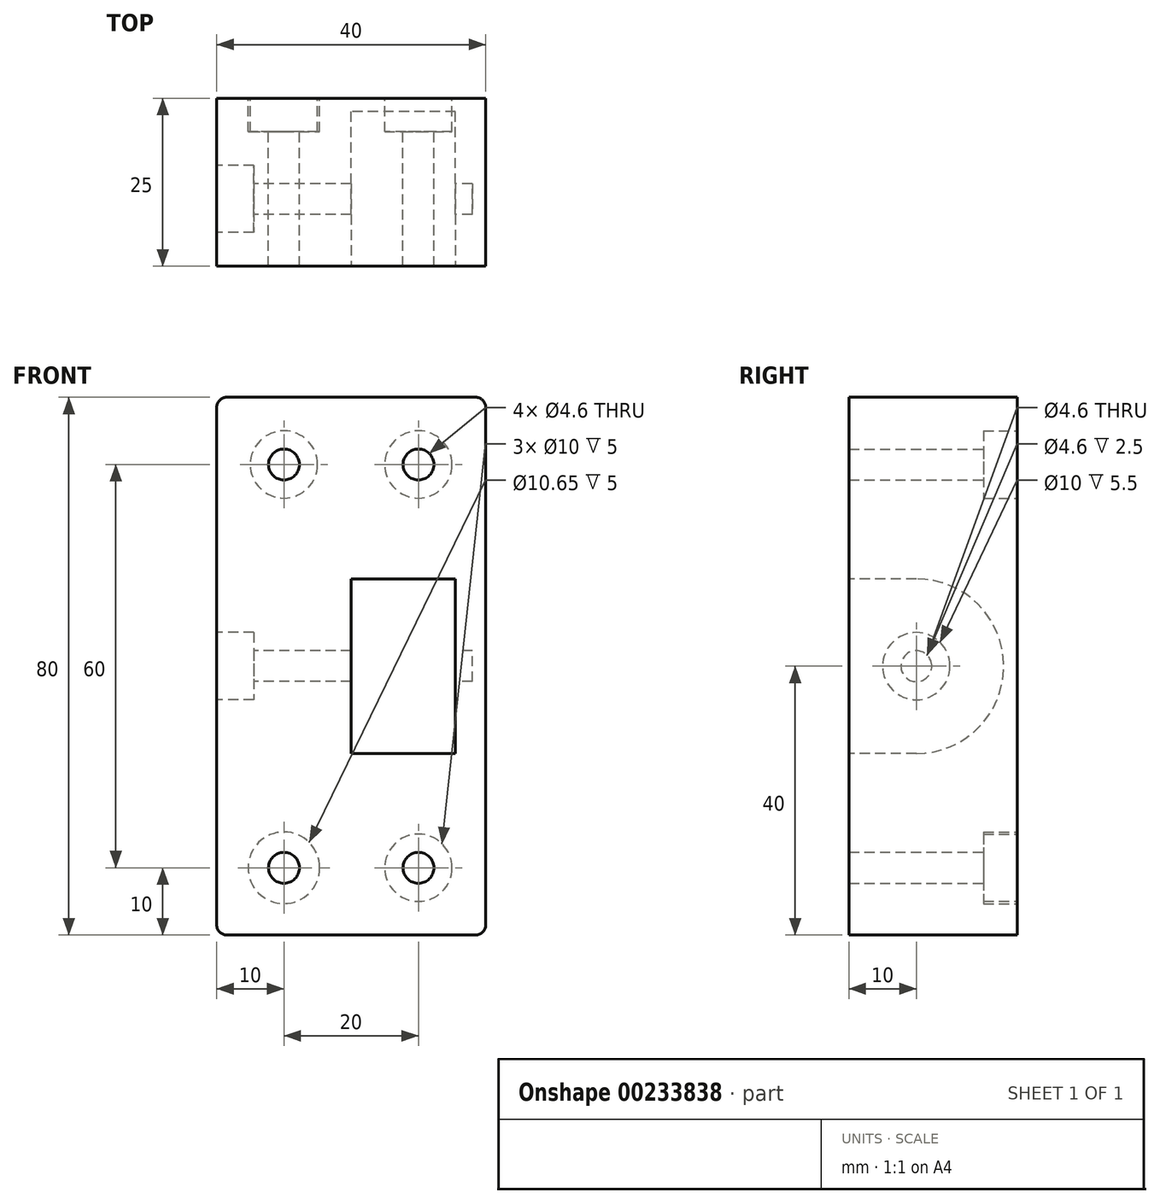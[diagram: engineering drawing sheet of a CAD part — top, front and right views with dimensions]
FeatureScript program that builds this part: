
annotation { "Feature Type Name" : "Feature", "Feature Type Description" : "" }
export const myFeature = defineFeature(function(context is Context, id is Id, definition is map)
    precondition{}
    {
        {
            var Q0;
            Q0=qCreatedBy(makeId("Front.planeOp"),FACE);
            var sketch = newSketch(context, id + "F0", { "sketchPlane" : qUnion([Q0])});
            skArc(sketch, "E0.0.89", {"start": v(20, -38.5) * mm, "mid": v(19.56, -39.56) * mm, "end": v(18.5, -40) * mm});
            skArc(sketch, "E0.0.121", {"start": v(-18.5, -40) * mm, "mid": v(-19.56, -39.56) * mm, "end": v(-20, -38.5) * mm});
            skArc(sketch, "E0.0.183", {"start": v(-20, 38.5) * mm, "mid": v(-19.56, 39.56) * mm, "end": v(-18.5, 40) * mm});
            skArc(sketch, "E0.0.215", {"start": v(18.5, 40) * mm, "mid": v(19.56, 39.56) * mm, "end": v(20, 38.5) * mm});
            skLineSegment(sketch, "E1", {"start": v(18.5, 40) * mm, "end": v(-18.5, 40) * mm});
            skLineSegment(sketch, "E2", {"start": v(-20, 38.5) * mm, "end": v(-20, -38.5) * mm});
            skLineSegment(sketch, "E3", {"start": v(-18.5, -40) * mm, "end": v(18.5, -40) * mm});
            skCircle(sketch, "E4.0", {"center": v(10, -30) * mm, "radius": 2.3 * mm});
            skCircle(sketch, "E4.1", {"center": v(-10, -30) * mm, "radius": 2.3 * mm});
            skCircle(sketch, "E4.4", {"center": v(-10, 30) * mm, "radius": 2.3 * mm});
            skCircle(sketch, "E4.5", {"center": v(10, 30) * mm, "radius": 2.3 * mm});
            skLineSegment(sketch, "E5", {"start": v(20, -38.5) * mm, "end": v(20, 38.5) * mm});
            skLineSegment(sketch, "E6", {"start": v(0, 40) * mm, "end": v(0, -40) * mm, "construction": true});
            skLineSegment(sketch, "E7", {"start": v(-20, 0) * mm, "end": v(20, 0) * mm, "construction": true});
            skPoint(sketch, "E8", {"position": v(0, 0) * mm});
            skSolve(sketch);
        }
        {
            var Q0;
            Q0 = qSketchRegion(id + "F0", true);
            extrude(context, id + "F1", {"entities" : qUnion([Q0]), "depth" : 25 * mm});
        }
        {
            var Q0;
            Q0=makeQuery(id+"F1.opExtrude","CAP_FACE",FACE,{"disambiguationData":[OSD([sQuery(id+"F0.wireOp",EDGE,"E0.0.89"),sQuery(id+"F0.wireOp",EDGE,"E0.0.121"),sQuery(id+"F0.wireOp",EDGE,"E0.0.183"),sQuery(id+"F0.wireOp",EDGE,"E0.0.215"),sQuery(id+"F0.wireOp",EDGE,"E1"),sQuery(id+"F0.wireOp",EDGE,"E2"),sQuery(id+"F0.wireOp",EDGE,"E3"),sQuery(id+"F0.wireOp",EDGE,"E4.0"),sQuery(id+"F0.wireOp",EDGE,"E4.1"),sQuery(id+"F0.wireOp",EDGE,"E4.4"),sQuery(id+"F0.wireOp",EDGE,"E4.5"),sQuery(id+"F0.wireOp",EDGE,"E5")])],"isStart":true});
            var sketch = newSketch(context, id + "F2", { "sketchPlane" : qUnion([Q0])});
            skCircle(sketch, "E9", {"center": v(-10, 30) * mm, "radius": 5 * mm});
            skCircle(sketch, "E10", {"center": v(10, 30) * mm, "radius": 5 * mm});
            skCircle(sketch, "E11", {"center": v(10, -30) * mm, "radius": 5.33 * mm});
            skCircle(sketch, "E12", {"center": v(-10, -30) * mm, "radius": 5 * mm});
            skSolve(sketch);
        }
        {
            var Q0;
            Q0 = qSketchRegion(id + "F2", true);
            extrude(context, id + "F3", {"entities" : qUnion([Q0]), "operationType" : NewBodyOperationType.REMOVE, "oppositeDirection" : true, "depth" : 5 * mm});
        }
        {
            var Q0;
            Q0=makeQuery(id+"F1.opExtrude","SWEPT_FACE",FACE,{"disambiguationData":[OSD([sQuery(id+"F0.wireOp",EDGE,"E2")])]});
            cPlane(context, id + "F4", {"entities" : qUnion([Q0]), "cplaneType" : CPlaneType.OFFSET, "offset" : 20 * mm, "oppositeDirection" : true, "width" : 150 * mm, "height" : 150 * mm});
        }
        {
            var Q0;
            Q0=makeQuery(id+"F1.opExtrude","SWEPT_FACE",FACE,{"disambiguationData":[OSD([sQuery(id+"F0.wireOp",EDGE,"E5")])]});
            cPlane(context, id + "F5", {"entities" : qUnion([Q0]), "cplaneType" : CPlaneType.OFFSET, "offset" : 4.5 * mm, "oppositeDirection" : true, "width" : 150 * mm, "height" : 150 * mm});
        }
        {
            var Q0;
            Q0=qCreatedBy(id+"F4.planeOp",FACE);
            var sketch = newSketch(context, id + "F6", { "sketchPlane" : qUnion([Q0])});
            skLineSegment(sketch, "E13.0", {"start": v(25, -13) * mm, "end": v(25, 13) * mm});
            skCircle(sketch, "E14", {"center": v(15, 0) * mm, "radius": 11 * mm, "construction": true});
            skArc(sketch, "E15", {"start": v(15, 13) * mm, "mid": v(2, 0) * mm, "end": v(15, -13) * mm});
            skLineSegment(sketch, "E16", {"start": v(15, 23.32) * mm, "end": v(15, -22.19) * mm, "construction": true});
            skLineSegment(sketch, "E17", {"start": v(15, 13) * mm, "end": v(25, 13) * mm});
            skLineSegment(sketch, "E18", {"start": v(15, -13) * mm, "end": v(25, -13) * mm});
            skPoint(sketch, "E19.orphan", {"position": v(25, -38.5) * mm});
            skPoint(sketch, "E20.orphan", {"position": v(25, 38.5) * mm});
            skSolve(sketch);
        }
        {
            var Q0;
            Q0 = qSketchRegion(id + "F6", true);
            var Q1;
            Q1=qCreatedBy(id+"F5.planeOp",FACE);
            extrude(context, id + "F7", {"entities" : qUnion([Q0]), "operationType" : NewBodyOperationType.REMOVE, "endBound" : BoundingType.UP_TO_SURFACE, "oppositeDirection" : true, "endBoundEntityFace" : qUnion([Q1]), "depth" : 25 * mm});
        }
        {
            var Q0;
            Q0=makeQuery(id+"F1.opExtrude","SWEPT_FACE",FACE,{"disambiguationData":[OSD([sQuery(id+"F0.wireOp",EDGE,"E5")])]});
            cPlane(context, id + "F8", {"entities" : qUnion([Q0]), "cplaneType" : CPlaneType.OFFSET, "offset" : 2 * mm, "oppositeDirection" : true, "width" : 150 * mm, "height" : 150 * mm});
        }
        {
            var Q0;
            Q0=makeQuery(id+"F1.opExtrude","SWEPT_FACE",FACE,{"disambiguationData":[OSD([sQuery(id+"F0.wireOp",EDGE,"E2")])]});
            var sketch = newSketch(context, id + "F9", { "sketchPlane" : qUnion([Q0])});
            skArc(sketch, "E21.0", {"start": v(15, 13) * mm, "mid": v(2, 0) * mm, "end": v(15, -13) * mm, "construction": true});
            skCircle(sketch, "E22", {"center": v(15, 0) * mm, "radius": 2.3 * mm});
            skSolve(sketch);
        }
        {
            var Q0;
            Q0 = qSketchRegion(id + "F9", true);
            var Q1;
            Q1=qCreatedBy(id+"F8.planeOp",FACE);
            extrude(context, id + "F10", {"entities" : qUnion([Q0]), "operationType" : NewBodyOperationType.REMOVE, "endBound" : BoundingType.UP_TO_SURFACE, "oppositeDirection" : true, "endBoundEntityFace" : qUnion([Q1]), "depth" : 25 * mm});
        }
        {
            var Q0;
            Q0=makeQuery(id+"F1.opExtrude","SWEPT_FACE",FACE,{"disambiguationData":[OSD([sQuery(id+"F0.wireOp",EDGE,"E2")])]});
            var sketch = newSketch(context, id + "F11", { "sketchPlane" : qUnion([Q0])});
            skCircle(sketch, "E23", {"center": v(15, 0) * mm, "radius": 5 * mm});
            skSolve(sketch);
        }
        {
            var Q0;
            Q0 = qSketchRegion(id + "F11", true);
            extrude(context, id + "F12", {"entities" : qUnion([Q0]), "operationType" : NewBodyOperationType.REMOVE, "oppositeDirection" : true, "depth" : 5.5 * mm});
        }
    });
